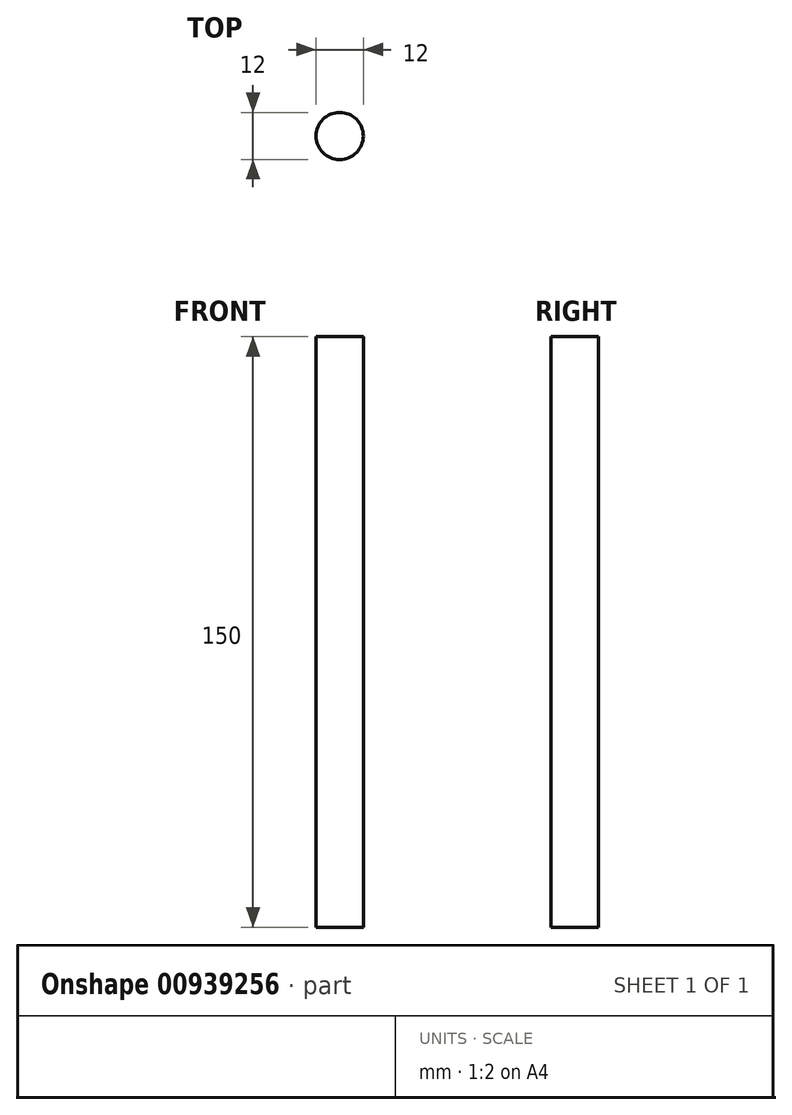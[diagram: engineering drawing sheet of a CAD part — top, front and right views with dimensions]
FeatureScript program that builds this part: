
annotation { "Feature Type Name" : "Feature", "Feature Type Description" : "" }
export const myFeature = defineFeature(function(context is Context, id is Id, definition is map)
    precondition{}
    {
        {
            var Q0;
            Q0=qCreatedBy(makeId("Top.planeOp"),FACE);
            var sketch = newSketch(context, id + "F0", { "sketchPlane" : qUnion([Q0])});
            skCircle(sketch, "E0", {"center": v(0, 0) * mm, "radius": 6 * mm});
            skSolve(sketch);
        }
        {
            var Q0;
            Q0=qCreatedBy(makeId("Front.planeOp"),FACE);
            var sketch = newSketch(context, id + "F1", { "sketchPlane" : qUnion([Q0])});
            skLineSegment(sketch, "E1", {"start": v(0, 0) * mm, "end": v(0, 150) * mm});
            skSolve(sketch);
        }
        {
            var Q0;
            Q0=makeQuery(id+"F0.imprint","IMPRINT",FACE,{"disambiguationData":[TD([[makeQuery(id+"F0.imprint","IMPRINT",EDGE,{"derivedFrom":sQuery(id+"F0.wireOp",EDGE,"E0")}),1.0]])]});
            var Q1;
            Q1=sQuery(id+"F1.wireOp",EDGE,"E1");
            sweep(context, id + "F2", {"profiles" : qUnion([Q0]), "path" : qUnion([Q1])});
        }
    });
